FCSTD DOCUMENT  (FreeCAD 0.19R)
Label: test1
License: All rights reserved
LicenseURL: http://en.wikipedia.org/wiki/All_rights_reserved
objects: App::TextDocument×1

FEATURE [App::TextDocument] Text_document  label="Text document"
  Text = %\nO00010 (KONTUR GRUBO)\n(PLUNJER ISCAR) \nG00 G17 G40 G49 G80 G90 \nG54 \nG52 X [ 0. ] Y [ 0. ] Z [ 0. ] \n\nT20 D20 M06 \nG43 H20 Z150. \nS2500 M03 \n#10= 3000. (PODA4A mm.) \n \n#1= 0. (NA4ALO) \n#2= -14. (KONEZ) \n#3= 0.5 (SHAG) \n#4= 16. / 2 (R INSTR) \n#5= 0.1 (OFFN) \n\n#6= 160. (X) \n#7= 40. (Y) \n#8= 10. (FASKA) \n#9= #7 / 2. + #4 + #5 + 10. (OTYEZD) \n#15= 0.1 (OTSTUP) \n\nG00 X [ #6 / 2. - #8 - #15 ] Y [ #9 ] \nG00 Z10. M08 \nG01 Z#1 F#10 \n\nWHILE [ #1 GT #2 ] DO1 \n#1= #1 - #3 \nIF [ #1 LT #2 ] THEN #1= #2 \n \nG01 X [ #6 / 2. - #8 + #5 - #15 ] Y [ #9 ] \nG01 Z [ #1 ] \nG01 G41 Y [ #7 / 2. + #5 ] F [ #10 / 2. ] \nG01 X [ #6 / 2. - #8 + #5 ] F#10 \nG01 X [ #6 / 2. + #5 ] Y [ #7 / 2. - #8 + #5 ] \nG01 Y [ - #7 / 2. + #8 - #5 ] \nG01 X [ #6 / 2. - #8 + #5 ] Y [ - #7 / 2. - #5 ] \nG01 X [ - #6 / 2. + #8 - #5 ] \nG01 X [ - #6 / 2. - #5 ] Y [ - #7 / 2. + #8 - #5 ] \nG01 Y [ #7 / 2. - #8 + #5 ] \nG01 X [ - #6 / 2. + #8 - #5 ] Y [ #7 / 2. + #5 ] \nG01 X [ #6 / 2. - #8 + #5 - #15 ] \nG01 G40 Y [ #9 ] \n\nEND1 \nG00 Z150. M09 \nM05 \nG52 X0. Y0. Z0. \nM99 \n\n%
